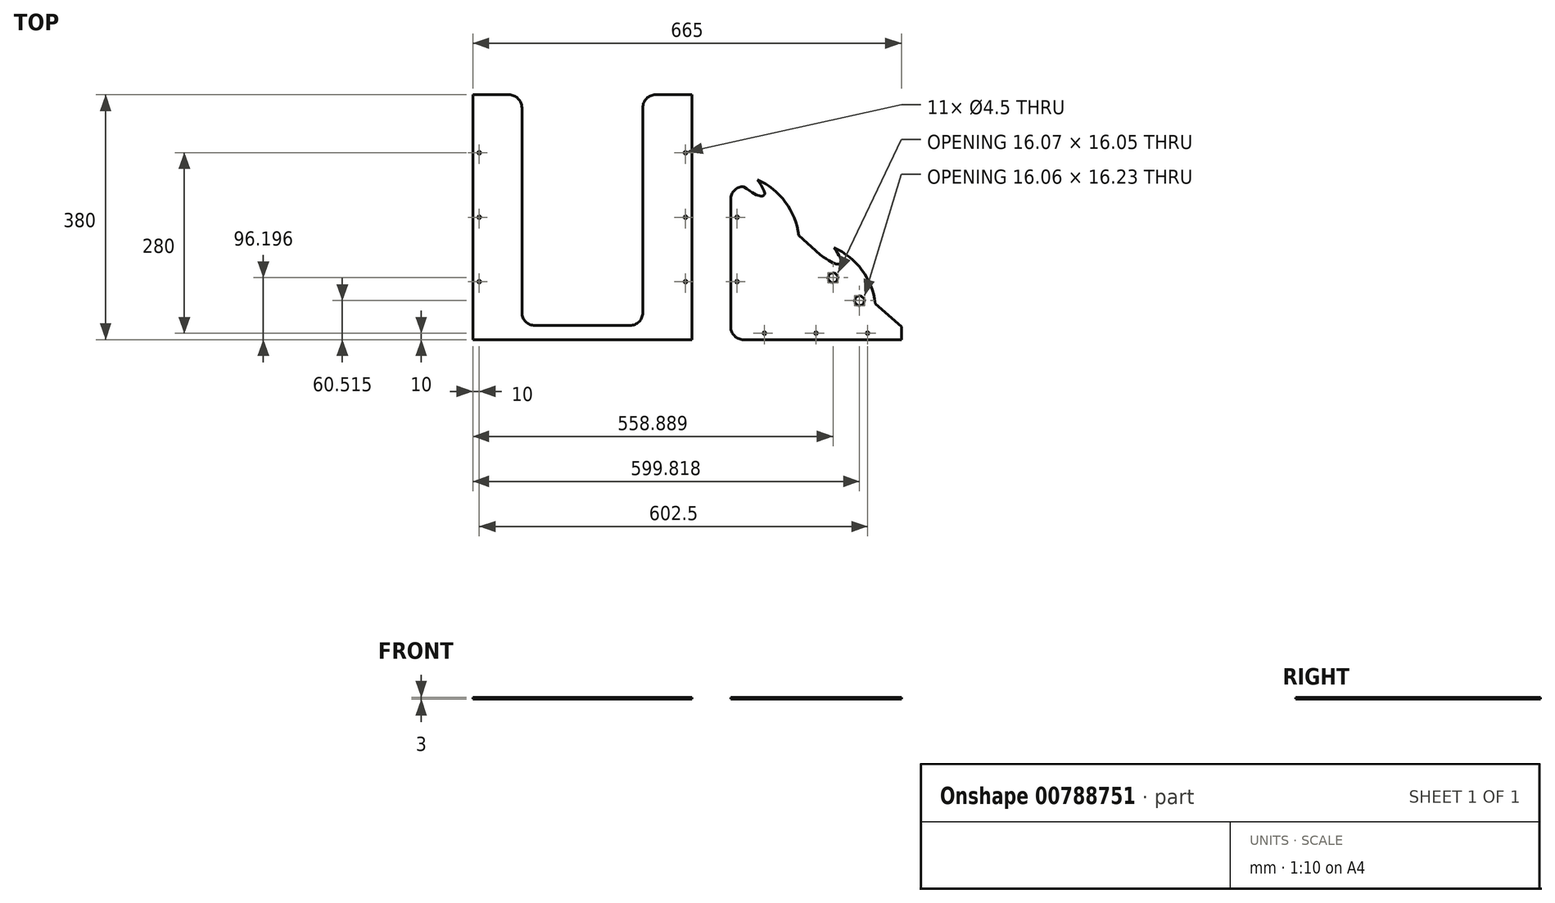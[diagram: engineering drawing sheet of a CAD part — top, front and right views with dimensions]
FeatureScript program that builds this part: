
annotation { "Feature Type Name" : "Feature", "Feature Type Description" : "" }
export const myFeature = defineFeature(function(context is Context, id is Id, definition is map)
    precondition{}
    {
        {
            var Q0;
            Q0=qCreatedBy(makeId("Top.planeOp"),FACE);
            var sketch = newSketch(context, id + "F0", { "sketchPlane" : qUnion([Q0])});
            skLineSegment(sketch, "E0", {"start": v(19.01, 251.06) * mm, "end": v(19.01, -128.94) * mm});
            skLineSegment(sketch, "E1", {"start": v(19.01, -128.94) * mm, "end": v(284.01, -128.94) * mm});
            skLineSegment(sketch, "E2", {"start": v(19.01, 251.06) * mm, "end": v(284.01, 251.06) * mm});
            skLineSegment(sketch, "E3", {"start": v(284.01, 251.06) * mm, "end": v(284.01, -128.94) * mm});
            skLineSegment(sketch, "E4.bottom", {"start": v(49.01, 211.06) * mm, "end": v(254.01, 211.06) * mm});
            skLineSegment(sketch, "E4.top", {"start": v(49.01, 203.06) * mm, "end": v(254.01, 203.06) * mm});
            skLineSegment(sketch, "E4.left", {"start": v(49.01, 211.06) * mm, "end": v(49.01, 203.06) * mm});
            skLineSegment(sketch, "E4.right", {"start": v(254.01, 211.06) * mm, "end": v(254.01, 203.06) * mm});
            skLineSegment(sketch, "E5", {"start": v(29.01, 251.06) * mm, "end": v(29.01, -128.94) * mm, "construction": true});
            skLineSegment(sketch, "E6", {"start": v(19.01, 241.06) * mm, "end": v(284.01, 241.06) * mm, "construction": true});
            skLineSegment(sketch, "E7", {"start": v(-380.99, -118.94) * mm, "end": v(-40.99, -118.94) * mm, "construction": true});
            skPoint(sketch, "E8", {"position": v(151.51, 241.06) * mm});
            skPoint(sketch, "E9", {"position": v(231.51, 241.06) * mm});
            skPoint(sketch, "E10", {"position": v(71.51, 241.06) * mm});
            skPoint(sketch, "E11", {"position": v(71.51, -118.94) * mm});
            skPoint(sketch, "E12", {"position": v(151.51, -118.94) * mm});
            skPoint(sketch, "E13", {"position": v(231.51, -118.94) * mm});
            skPoint(sketch, "E14", {"position": v(29.01, 61.06) * mm});
            skPoint(sketch, "E15", {"position": v(29.01, 161.06) * mm});
            skPoint(sketch, "E16", {"position": v(29.01, -38.94) * mm});
            skLineSegment(sketch, "E17.bottom", {"start": v(-40.99, 251.06) * mm, "end": v(-380.99, 251.06) * mm});
            skLineSegment(sketch, "E17.top", {"start": v(-40.99, -128.94) * mm, "end": v(-380.99, -128.94) * mm});
            skLineSegment(sketch, "E17.left", {"start": v(-40.99, 251.06) * mm, "end": v(-40.99, -128.94) * mm});
            skLineSegment(sketch, "E17.right", {"start": v(-380.99, 251.06) * mm, "end": v(-380.99, -128.94) * mm});
            skLineSegment(sketch, "E18", {"start": v(-370.99, 251.06) * mm, "end": v(-370.99, -128.94) * mm, "construction": true});
            skLineSegment(sketch, "E19", {"start": v(-50.99, 251.06) * mm, "end": v(-50.99, -128.94) * mm, "construction": true});
            skPoint(sketch, "E20", {"position": v(-50.99, 161.06) * mm});
            skPoint(sketch, "E21", {"position": v(-370.99, 161.06) * mm});
            skPoint(sketch, "E22", {"position": v(-50.99, -38.94) * mm});
            skPoint(sketch, "E23", {"position": v(-370.99, -38.94) * mm});
            skPoint(sketch, "E24", {"position": v(-370.99, 61.06) * mm});
            skPoint(sketch, "E25", {"position": v(-50.99, 61.06) * mm});
            skPoint(sketch, "E26.orphan", {"position": v(19.01, -118.94) * mm});
            skLineSegment(sketch, "E27.trimOffspring", {"start": v(19.01, -118.94) * mm, "end": v(284.01, -118.94) * mm, "construction": true});
            skLineSegment(sketch, "E28.bottom", {"start": v(-304.74, 277.8) * mm, "end": v(-117.24, 277.8) * mm});
            skLineSegment(sketch, "E28.top", {"start": v(-304.74, -106.94) * mm, "end": v(-117.24, -106.94) * mm});
            skLineSegment(sketch, "E28.left", {"start": v(-304.74, 277.8) * mm, "end": v(-304.74, -106.94) * mm});
            skLineSegment(sketch, "E28.right", {"start": v(-117.24, 277.8) * mm, "end": v(-117.24, -106.94) * mm});
            skPoint(sketch, "E28.middle", {"position": v(-210.99, 85.43) * mm});
            skLineSegment(sketch, "E29", {"start": v(-210.99, 85.43) * mm, "end": v(-210.99, 251.06) * mm, "construction": true});
            skLineSegment(sketch, "E30", {"start": v(19.01, 108.69) * mm, "end": v(39.01, 108.69) * mm});
            skPoint(sketch, "E31", {"position": v(284.01, -108.94) * mm});
            skLineSegment(sketch, "E32", {"start": v(39.01, 108.69) * mm, "end": v(284.01, -108.94) * mm, "construction": true});
            skArc(sketch, "E33", {"start": v(124.68, 32.6) * mm, "mid": v(104, 84.37) * mm, "end": v(60.6, 119.37) * mm});
            skFitSpline(sketch, "E34", {"points": [v(39.01, 108.69) * mm, v(70.63, 94.94) * mm, v(60.6, 119.37) * mm], "startDerivative": vector(118.36, -91.2) * mm, "endDerivative": vector(-77.57, 115.07) * mm});
            skArc(sketch, "E35", {"start": v(243.5, -72.95) * mm, "mid": v(222.83, -21.17) * mm, "end": v(179.42, 13.82) * mm});
            skFitSpline(sketch, "E36", {"points": [v(157.83, 3.14) * mm, v(189.45, -10.6) * mm, v(179.42, 13.82) * mm], "startDerivative": vector(118.36, -91.2) * mm, "endDerivative": vector(-77.57, 115.07) * mm});
            skLineSegment(sketch, "E37", {"start": v(124.68, 32.6) * mm, "end": v(157.83, 3.14) * mm});
            skLineSegment(sketch, "E38", {"start": v(243.5, -72.95) * mm, "end": v(284.01, -108.94) * mm});
            skCircle(sketch, "E39.cCircle", {"center": v(177.9, -32.74) * mm, "radius": 7.2 * mm, "construction": true});
            skLineSegment(sketch, "E39.0", {"start": v(175.72, -40.77) * mm, "end": v(183.76, -38.64) * mm});
            skLineSegment(sketch, "E39.1", {"start": v(169.86, -34.87) * mm, "end": v(175.72, -40.77) * mm});
            skLineSegment(sketch, "E39.2", {"start": v(172.04, -26.85) * mm, "end": v(169.86, -34.87) * mm});
            skLineSegment(sketch, "E39.3", {"start": v(180.07, -24.72) * mm, "end": v(172.04, -26.85) * mm});
            skLineSegment(sketch, "E39.4", {"start": v(185.94, -30.62) * mm, "end": v(180.07, -24.72) * mm});
            skLineSegment(sketch, "E39.5", {"start": v(183.76, -38.64) * mm, "end": v(185.94, -30.62) * mm});
            skPoint(sketch, "E39.0.midPoint", {"position": v(179.74, -39.7) * mm});
            skCircle(sketch, "E40.cCircle", {"center": v(218.83, -68.42) * mm, "radius": 7.24 * mm, "construction": true});
            skLineSegment(sketch, "E40.0", {"start": v(220.83, -60.3) * mm, "end": v(226.86, -66.1) * mm});
            skLineSegment(sketch, "E40.1", {"start": v(226.86, -66.1) * mm, "end": v(224.86, -74.21) * mm});
            skLineSegment(sketch, "E40.2", {"start": v(224.86, -74.21) * mm, "end": v(216.83, -76.54) * mm});
            skLineSegment(sketch, "E40.3", {"start": v(216.83, -76.54) * mm, "end": v(210.8, -70.75) * mm});
            skLineSegment(sketch, "E40.4", {"start": v(210.8, -70.75) * mm, "end": v(212.8, -62.63) * mm});
            skLineSegment(sketch, "E40.5", {"start": v(212.8, -62.63) * mm, "end": v(220.83, -60.3) * mm});
            skPoint(sketch, "E40.0.midPoint", {"position": v(223.84, -63.2) * mm});
            skSolve(sketch);
        }
        {
            var Q0;
            Q0=makeQuery(id+"F0.imprint","IMPRINT",FACE,{"disambiguationData":[TD([[makeQuery(id+"F0.imprint","IMPRINT",EDGE,{"derivedFrom":sQuery(id+"F0.wireOp",EDGE,"E17.top")}),-1.0]])]});
            var Q1;
            {var subQ2=sQuery(id+"F0.wireOp",EDGE,"E1");Q1=makeQuery(id+"F0.imprint","IMPRINT",FACE,{"disambiguationData":[TD([[makeQuery(id+"F0.imprint","IMPRINT",EDGE,{"derivedFrom":subQ2}),1.0]])]});}
            extrude(context, id + "F1", {"entities" : qUnion([Q0, Q1]), "depth" : 3 * mm, "offsetDistance" : 25 * mm});
        }
        {
            var Q0;
            Q0=sQuery(id+"F0.wireOp",VERTEX,"E16");
            var Q1;
            Q1=sQuery(id+"F0.wireOp",VERTEX,"E11");
            var Q2;
            Q2=sQuery(id+"F0.wireOp",VERTEX,"E14");
            var Q3;
            Q3=sQuery(id+"F0.wireOp",VERTEX,"E15");
            var Q4;
            Q4=sQuery(id+"F0.wireOp",VERTEX,"E10");
            var Q5;
            Q5=sQuery(id+"F0.wireOp",VERTEX,"E8");
            var Q6;
            Q6=sQuery(id+"F0.wireOp",VERTEX,"E9");
            var Q7;
            Q7=sQuery(id+"F0.wireOp",VERTEX,"E12");
            var Q8;
            Q8=sQuery(id+"F0.wireOp",VERTEX,"E13");
            var Q9;
            Q9=sQuery(id+"F0.wireOp",VERTEX,"E20");
            var Q10;
            Q10=sQuery(id+"F0.wireOp",VERTEX,"E25");
            var Q11;
            Q11=sQuery(id+"F0.wireOp",VERTEX,"E22");
            var Q12;
            Q12=sQuery(id+"F0.wireOp",VERTEX,"E23");
            var Q13;
            Q13=sQuery(id+"F0.wireOp",VERTEX,"E24");
            var Q14;
            Q14=sQuery(id+"F0.wireOp",VERTEX,"E21");
            var Q15;
            Q15=makeQuery(id+"F1.opExtrude","SWEPT_BODY",BODY,{"disambiguationData":[OSD([sQuery(id+"F0.wireOp",EDGE,"E0"),sQuery(id+"F0.wireOp",EDGE,"E1"),sQuery(id+"F0.wireOp",EDGE,"E2"),sQuery(id+"F0.wireOp",EDGE,"E3"),sQuery(id+"F0.wireOp",EDGE,"E4.bottom"),sQuery(id+"F0.wireOp",EDGE,"E4.top"),sQuery(id+"F0.wireOp",EDGE,"E4.left"),sQuery(id+"F0.wireOp",EDGE,"E4.right")])]});
            var Q16;
            Q16=makeQuery(id+"F1.opExtrude","SWEPT_BODY",BODY,{"disambiguationData":[OSD([sQuery(id+"F0.wireOp",EDGE,"E17.bottom"),sQuery(id+"F0.wireOp",EDGE,"E17.top"),sQuery(id+"F0.wireOp",EDGE,"E17.left"),sQuery(id+"F0.wireOp",EDGE,"E17.right"),sQuery(id+"F0.wireOp",EDGE,"E28.top"),sQuery(id+"F0.wireOp",EDGE,"E28.left"),sQuery(id+"F0.wireOp",EDGE,"E28.right")])]});
            hole(context, id + "F2", {"style" : HoleStyle.SIMPLE, "endStyle" : HoleEndStyle.BLIND, "oppositeDirection" : true, "holeDiameter" : 4.5 * mm, "majorDiameter" : 5 * mm, "holeDepth" : 50 * mm, "isTappedThrough" : true, "tappedDepth" : 12 * mm, "tapClearance" : 3, "locations" : qUnion([Q0, Q1, Q2, Q3, Q4, Q5, Q6, Q7, Q8, Q9, Q10, Q11, Q12, Q13, Q14]), "scope" : qUnion([Q15, Q16]), "startStyle" : HoleStartStyle.SKETCH});
        }
        {
            var Q0;
            Q0=makeQuery(id+"F1.opExtrude","SWEPT_EDGE",EDGE,{"disambiguationData":[OSD([sQuery(id+"F0.wireOp",EDGE,"E0"),sQuery(id+"F0.wireOp",EDGE,"E2")])]});
            var Q1;
            Q1=makeQuery(id+"F1.opExtrude","SWEPT_EDGE",EDGE,{"disambiguationData":[OSD([sQuery(id+"F0.wireOp",EDGE,"E0"),sQuery(id+"F0.wireOp",EDGE,"E1")])]});
            var Q2;
            Q2=makeQuery(id+"F1.opExtrude","SWEPT_EDGE",EDGE,{"disambiguationData":[OSD([sQuery(id+"F0.wireOp",EDGE,"E28.top"),sQuery(id+"F0.wireOp",EDGE,"E28.left")])]});
            var Q3;
            Q3=makeQuery(id+"F1.opExtrude","SWEPT_EDGE",EDGE,{"disambiguationData":[OSD([sQuery(id+"F0.wireOp",EDGE,"E28.top"),sQuery(id+"F0.wireOp",EDGE,"E28.right")])]});
            var Q4;
            Q4=makeQuery(id+"F1.opExtrude","SWEPT_EDGE",EDGE,{"disambiguationData":[OSD([sQuery(id+"F0.wireOp",EDGE,"E17.bottom"),sQuery(id+"F0.wireOp",EDGE,"E28.left")])]});
            var Q5;
            Q5=makeQuery(id+"F1.opExtrude","SWEPT_EDGE",EDGE,{"disambiguationData":[OSD([sQuery(id+"F0.wireOp",EDGE,"E17.bottom"),sQuery(id+"F0.wireOp",EDGE,"E28.right")])]});
            fillet(context, id + "F3", {"entities" : qUnion([Q0, Q1, Q2, Q3, Q4, Q5]), "tangentPropagation" : true, "radius" : 20 * mm, "defaultsChanged" : false, "vertexSettings" : [], "allowEdgeOverflow" : false});
        }
    });
